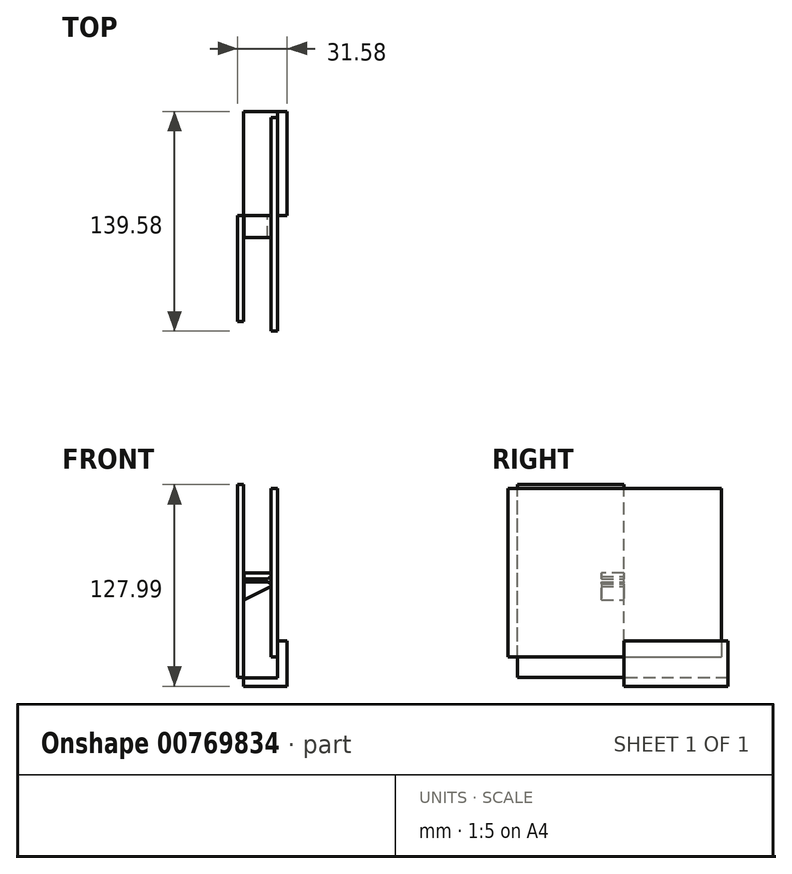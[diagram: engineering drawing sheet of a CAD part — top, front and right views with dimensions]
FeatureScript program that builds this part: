
annotation { "Feature Type Name" : "Feature", "Feature Type Description" : "" }
export const myFeature = defineFeature(function(context is Context, id is Id, definition is map)
    precondition{}
    {
        {
            var Q0;
            Q0=qCreatedBy(makeId("Right.planeOp"),FACE);
            var sketch = newSketch(context, id + "F0", { "sketchPlane" : qUnion([Q0])});
            skLineSegment(sketch, "E0.bottom", {"start": v(-73.54, 53.73) * mm, "end": v(62, 53.73) * mm});
            skLineSegment(sketch, "E0.top", {"start": v(-73.54, -53.53) * mm, "end": v(62, -53.53) * mm});
            skLineSegment(sketch, "E0.left", {"start": v(-73.54, 53.73) * mm, "end": v(-73.54, -53.53) * mm});
            skLineSegment(sketch, "E0.right", {"start": v(62, 53.73) * mm, "end": v(62, -53.53) * mm});
            skSolve(sketch);
        }
        {
            var Q0;
            Q0=makeQuery(id+"F0.imprint","IMPRINT",FACE,{"disambiguationData":[TD([[makeQuery(id+"F0.imprint","IMPRINT",EDGE,{"derivedFrom":sQuery(id+"F0.wireOp",EDGE,"E0.bottom")}),-1.0]])]});
            extrude(context, id + "F1", {"entities" : qUnion([Q0]), "oppositeDirection" : true, "depth" : 4.32 * mm, "offsetDistance" : 25.4 * mm});
        }
        {
            var Q0;
            Q0=qCreatedBy(makeId("Front.planeOp"),FACE);
            var sketch = newSketch(context, id + "F2", { "sketchPlane" : qUnion([Q0])});
            skLineSegment(sketch, "E1", {"start": v(0, -43.3) * mm, "end": v(0, -66.67) * mm});
            skLineSegment(sketch, "E2", {"start": v(0, -66.67) * mm, "end": v(-21.59, -66.67) * mm});
            skLineSegment(sketch, "E3", {"start": v(-21.59, -66.67) * mm, "end": v(-21.59, -71.97) * mm});
            skLineSegment(sketch, "E4", {"start": v(-21.59, -71.97) * mm, "end": v(6.09, -71.97) * mm});
            skLineSegment(sketch, "E5", {"start": v(6.09, -71.97) * mm, "end": v(6.09, -43.14) * mm});
            skLineSegment(sketch, "E6", {"start": v(6.09, -43.14) * mm, "end": v(0, -43.3) * mm});
            skSolve(sketch);
        }
        {
            var Q0;
            Q0=qCreatedBy(makeId("Front.planeOp"),FACE);
            var sketch = newSketch(context, id + "F3", { "sketchPlane" : qUnion([Q0])});
            skLineSegment(sketch, "E7.bottom", {"start": v(-21.83, -66.4) * mm, "end": v(-25.49, -66.4) * mm});
            skLineSegment(sketch, "E7.top", {"start": v(-21.83, 56.02) * mm, "end": v(-25.49, 56.02) * mm});
            skLineSegment(sketch, "E7.left", {"start": v(-21.83, -66.4) * mm, "end": v(-21.83, 56.02) * mm});
            skLineSegment(sketch, "E7.right", {"start": v(-25.49, -66.4) * mm, "end": v(-25.49, 56.02) * mm});
            skSolve(sketch);
        }
        {
            var Q0;
            Q0 = qSketchRegion(id + "F3", true);
            extrude(context, id + "F4", {"entities" : qUnion([Q0]), "depth" : 67.56 * mm, "offsetDistance" : 25.4 * mm});
        }
        {
            var Q0;
            Q0=makeQuery(id+"F2.imprint","IMPRINT",FACE,{"disambiguationData":[TD([[makeQuery(id+"F2.imprint","IMPRINT",EDGE,{"derivedFrom":sQuery(id+"F2.wireOp",EDGE,"E1")}),1.0]])]});
            extrude(context, id + "F5", {"entities" : qUnion([Q0]), "operationType" : NewBodyOperationType.ADD, "oppositeDirection" : true, "depth" : 66.04 * mm, "offsetDistance" : 25.4 * mm});
        }
        {
            var Q0;
            Q0=qCreatedBy(makeId("Front.planeOp"),FACE);
            var sketch = newSketch(context, id + "F6", { "sketchPlane" : qUnion([Q0])});
            skLineSegment(sketch, "E8", {"start": v(-21.52, 0) * mm, "end": v(-3.95, 0) * mm});
            skLineSegment(sketch, "E9", {"start": v(-3.95, 0) * mm, "end": v(-3.95, -8.6) * mm});
            skLineSegment(sketch, "E10", {"start": v(-3.95, -8.6) * mm, "end": v(-21.35, -17.06) * mm});
            skLineSegment(sketch, "E11", {"start": v(-21.35, -17.06) * mm, "end": v(-21.52, 0) * mm});
            skLineSegment(sketch, "E12", {"start": v(-3.95, -1.96) * mm, "end": v(-3.95, -7.23) * mm});
            skLineSegment(sketch, "E13", {"start": v(-3.95, -7.23) * mm, "end": v(-6.55, -5.82) * mm});
            skLineSegment(sketch, "E14", {"start": v(-6.55, -5.82) * mm, "end": v(-29.63, -6.05) * mm});
            skLineSegment(sketch, "E15", {"start": v(-3.95, -1.96) * mm, "end": v(-6.31, -3.71) * mm});
            skLineSegment(sketch, "E16", {"start": v(-6.31, -3.71) * mm, "end": v(-29.4, -3.71) * mm});
            skLineSegment(sketch, "E17", {"start": v(-29.4, -3.71) * mm, "end": v(-33.03, -5.35) * mm});
            skLineSegment(sketch, "E18", {"start": v(-33.03, -5.35) * mm, "end": v(-29.63, -6.05) * mm});
            skSolve(sketch);
        }
        {
            var Q0;
            {var subQ1=sQuery(id+"F6.wireOp",EDGE,"E8");Q0=makeQuery(id+"F6.imprint","IMPRINT",FACE,{"disambiguationData":[TD([[makeQuery(id+"F6.imprint","IMPRINT",EDGE,{"derivedFrom":subQ1}),-1.0]])]});}
            var Q1;
            {var subQ1=sQuery(id+"F6.wireOp",EDGE,"E10");Q1=makeQuery(id+"F6.imprint","IMPRINT",FACE,{"disambiguationData":[TD([[makeQuery(id+"F6.imprint","IMPRINT",EDGE,{"derivedFrom":subQ1}),-1.0]])]});}
            extrude(context, id + "F7", {"entities" : qUnion([Q0, Q1]), "operationType" : NewBodyOperationType.ADD, "depth" : 14.22 * mm, "offsetDistance" : 25.4 * mm});
        }
    });
